# Revit family: Bandschelle - MBS 120
name_source: partatom
category: Generic Models
revit_build: Autodesk Revit 2017 (Build: 20190508_0315(x64)
units: mm (PartAtom-declared; Revit-internal decimal feet)

## family parameters
Always vertical = Yes
Can host rebar = No
Cut with Voids When Loaded = No
Part Type = Normal
Room Calculation Point = No
Round Connector Dimension = Use Diameter
Shared = No
Work Plane-Based = No

## types (2) — shared parameters
Cut's number = 2
Cut's space = 5 mm  [stored 0.0164042 ft]
Manufacturer = OBO BETTERMANN
Material = Edelstahl, rostfrei 1.4301
URL = http://www.obo-bettermann.com
Width = 12 mm  [stored 0.0393701 ft]

## per-type parameters (varying)
| type | Cut's number 2 | GTIN | Length | Length 1 | Manufacturer Art.No. |
| MBS 120 | 240 | 4012195693406 | 1200 mm | 1200 mm | 7203112 |
| MBS 150 | 300 | 4012195693413 | 1500 mm  [stored 4.92126 ft] | 1500 mm  [stored 4.92126 ft] | 7203114 |

note: column(s) folded — value = type name in every type: Article Type

note: [stored X ft] marks values corroborated as IEEE doubles in the binary element streams (Revit-internal decimal feet)

## geometry (parser evidence)
native form markers: Sweep x1
no freeform markers — native parametric forms only
